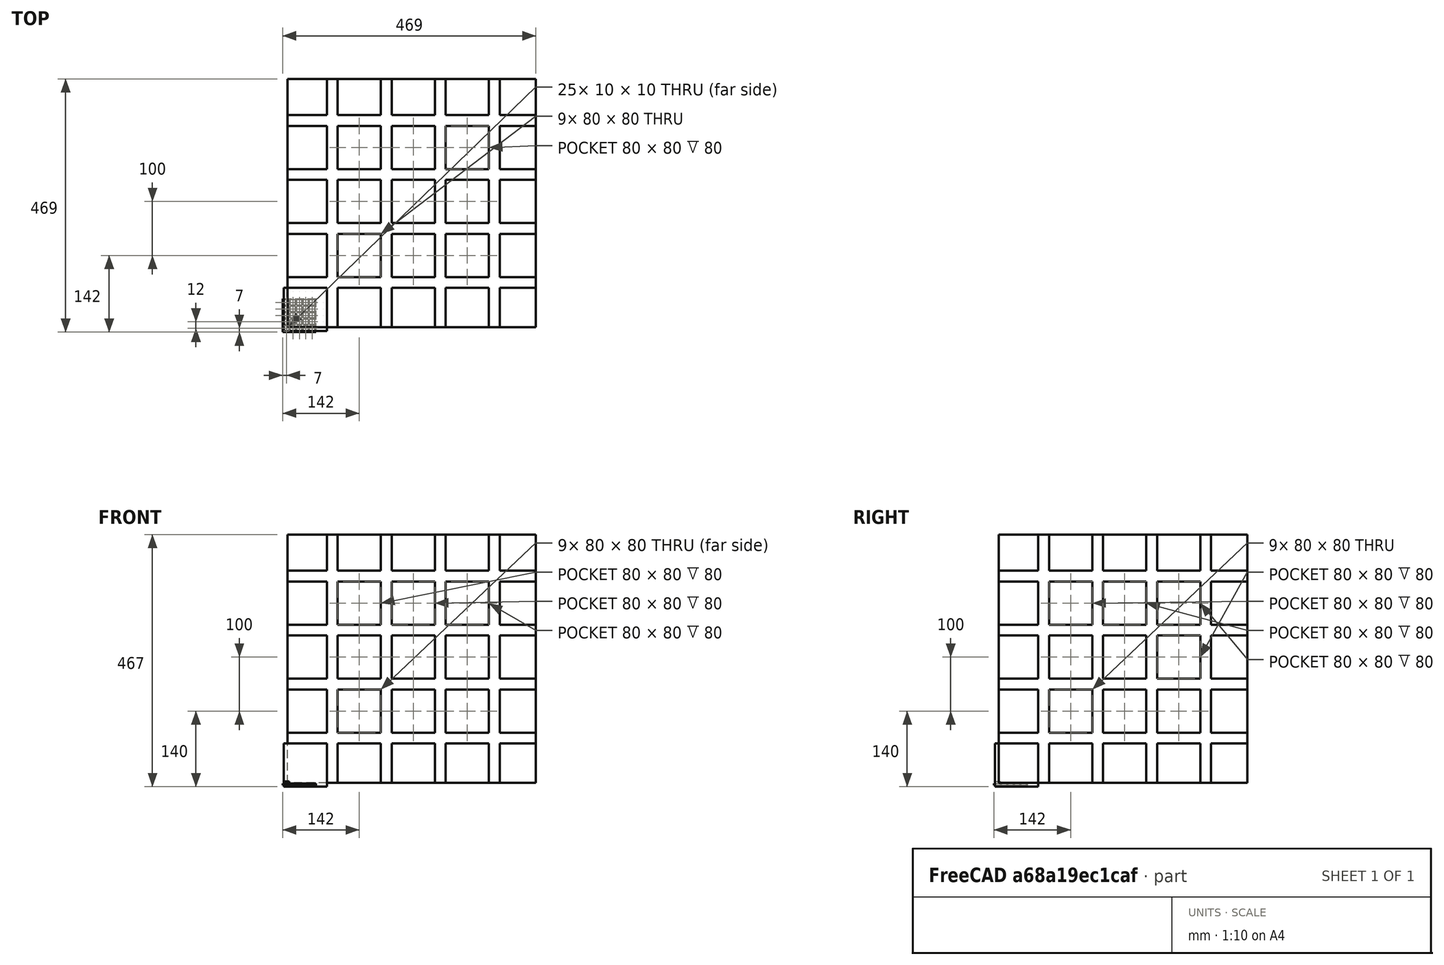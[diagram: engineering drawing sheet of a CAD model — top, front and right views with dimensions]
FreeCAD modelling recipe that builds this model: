
FCSTD DOCUMENT  (FreeCAD 1.0R39319 (Git))
Label: ojt1_t10p01_array
License: All rights reserved
LicenseURL: https://en.wikipedia.org/wiki/All_rights_reserved
objects: Part::Box×4, Part::FeaturePython×2, Part::Cut×2
note: 6 computed .brp shape members not serialized (recipe doc carries the construction recipe); baked Part::Feature solids carry a one-line shape summary decoded from their .brp

FEATURE [Part::Box] Box  label="Cub"
  AttacherType = Attacher::AttachEngine3D
  Height = 10
  Length = 10
  Width = 10
FEATURE [Part::FeaturePython] Array  # Draft array (typed FeaturePython)
  AlwaysSyncPlacement = false
  Angle = 360
  ArrayType = 0
  Axis = (0,0,1)
  Base = -> Box
  Center = (0,0,0)
  Count = 25
  ExpandArray = false
  Fuse = false
  IntervalAxis = (0,0,0)
  IntervalX = (12,0,0)
  IntervalY = (0,12,0)
  IntervalZ = (5,5,100)
  NumberCircles = 3
  NumberPolar = 5
  NumberX = 5
  NumberY = 5
  NumberZ = 1
  PlacementList = 25 placements: [(0,0,0),(0,12,0),(0,24,0),(0,36,0),(0,48,0),(12,0,0),(12,12,0),(12,24,0),(12,36,0),(12,48,0),(24,0,0),(24,12,0),(24,24,0),(24,36,0),(24,48,0),(36,0,0),(36,12,0),(36,24,0),(36,36,0),(36,48,0),(48,0,0),(48,12,0),(48,24,0),(48,36,0),(48,48,0)]
  RadialDistance = 50
  ScaleList = (25) [(1,1,1),(1,1,1),(1,1,1),(1,1,1),(1,1,1),(1,1,1),(1,1,1),(1,1,1),(1,1,1),(1,1,1),(1,1,1),(1,1,1),(1,1,1),(1,1,1),(1,1,1),(1,1,1),(1,1,1),(1,1,1),+7 more]
  Symmetry = 1
  TangentialDistance = 25
FEATURE [Part::Box] Box001  label="Cub001"
  AttacherType = Attacher::AttachEngine3D
  Height = 3
  Length = 62
  Placement = pos=(-2,-2,3) rot=(0,0,1;0rad)
  Width = 62
FEATURE [Part::Cut] Cut
  Base = -> Box001
  Refine = true
  Tool = -> Array
FEATURE [Part::Box] Box002  label="Cub002"
  AttacherType = Attacher::AttachEngine3D
  Height = 80
  Length = 80
  Width = 80
FEATURE [Part::FeaturePython] Array001  # Draft array (typed FeaturePython)
  AlwaysSyncPlacement = false
  Angle = 360
  ArrayType = 0
  Axis = (0,0,1)
  Base = -> Box002
  Center = (0,0,0)
  Count = 125
  ExpandArray = false
  Fuse = false
  IntervalAxis = (0,0,0)
  IntervalX = (100,0,0)
  IntervalY = (0,100,0)
  IntervalZ = (0,0,100)
  NumberCircles = 3
  NumberPolar = 5
  NumberX = 5
  NumberY = 5
  NumberZ = 5
  PlacementList = 125 placements: [(0,0,0),(0,0,100),(0,0,200),(0,0,300),(0,0,400),(0,100,0),(0,100,100),(0,100,200),(0,100,300),(0,100,400),(0,200,0),(0,200,100),(0,200,200),(0,200,300),(0,200,400),(0,300,0),(0,300,100),(0,300,200),(0,300,300),(0,300,400),(0,400,0),(0,400,100),(0,400,200),(0,400,300),(0,400,400),(100,0,0),(100,0,100),(100,0,200),(100,0,300),(100,0,400),(100,100,0),(100,100,100),(100,100,200),(100,100,300),+91 more]
  RadialDistance = 50
  Symmetry = 1
  TangentialDistance = 25
FEATURE [Part::Box] Box003  label="Cub003"
  AttacherType = Attacher::AttachEngine3D
  Height = 460
  Length = 460
  Placement = pos=(7,7,7) rot=(0,0,1;0rad)
  Width = 460
FEATURE [Part::Cut] Cut001
  Base = -> Box003
  Refine = true
  Tool = -> Array001
